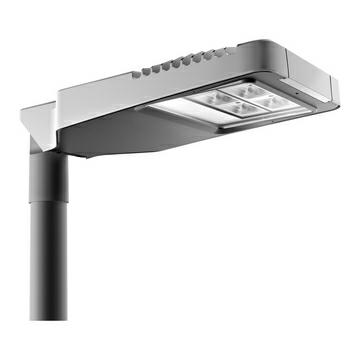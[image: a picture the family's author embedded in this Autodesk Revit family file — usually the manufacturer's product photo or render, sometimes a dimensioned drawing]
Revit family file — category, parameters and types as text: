
# Revit family: Lighting-StreetLighting-GEWISS-ROAD[5]MEDIUM-LED_OPTIC_WIDE-W_NEMA-ZAGA
name_source: partatom
category: Apparecchi per illuminazione
units: mm (PartAtom-declared; Revit-internal decimal feet)

## family parameters
Basato su piano di lavoro = No
Condiviso = No
Punto di calcolo locali = No
Quota connettore circolare = Usa diametro
Sempre verticale = Sì
Sorgente d'illuminazione = No
Taglio con vuoti quando caricato = No
Tipo di parte = Normale

## types (4) — shared parameters
Applicazione = External
Body = Die-cast aluminium -
Catalogue = LIGHTING
Catalogue Range = ROAD [5]
Classification: = -
Color Rendering Index = CRI-70
Colore = Graphite grey
Colour : = Powder coating
Colour temperature = 4000K
Colour temperature: = 4000 K (CRI>70)
Context = Street and parking lighting
DIN 18032-3 certification = -
Device with reduced surface temperature = -
Driver = Included
Driver Box = Built-in
Electrocod = 244C
Eletrical and lighting features = -
External screw = Stainless steel
Fixing = Pole Head - Outreach
Gasket = Anti-aging silicone
General information = -
Glow Wire Test : = -
IDF = ebad91c9-d513-4bb5-a7ee-f89ce0000d46
IDT = d586ed85c3ba44b3a220029348af3ca9
IP degree = IP66
Immagine tipo = GWR5276M.jpg
Installationa and maintenance = -
Insulation class = II
LED Life time (L80B10) = 100000H
LED Maintenance = Not available
LED current. = 0,5A
Lamp- = LED
Lampada = LED
Lifetime = L90B10 (Tq+25°C) = 100.000 h
Locking Hook = Integrated front handle
Luminaire = LED Road Equipment
Materials = -
Maximum surface exposed to the wind = 0,19M2
Maximum surface exposed to the wind : = 0.19 m2
Minimum distance from the illuminated object = 1M
Mouting and installation = Pole Head - Outreach
Operating temperature : = -25 +30 °C
Operating temperature: = -25 +30 °C
Optic = WIDE
Optic : = Metallized polycarbonate reflector
Optic Maintenance = Not available
Optic and illuminating features = -
Overvoltage protection = DM 10KV / CM 10KV
Overvoltage resistance = 10 KV (Common mode)
Photobiological Risk Class = RG0
Produttore = GEWISS S.p.A.
Rated frequency (Hz) = 50 / 60
SEO = Street lighting
Shield type = 4mm thick flat tempered glass
Shock resistance = IK08
Standard Deviation Colour Matching = SDCM = 5
Standard- = EN 60598-2-3, EN 60598-1 IEC/TR 62778
Standards and approvals = -
Stocking temperature = -
Supply voltage = 220 - 240 V
Technical sheet = https://www.gewiss.com
Tilt adjustable = -20° ÷ +10° side bracket - -10° ÷ +20° pole head
Tilt- = -20° ÷ +10° side bracket - -10° ÷ +20° pole head
Tipo alimentatore = Constant Current Driver Led
Tipologia = Bi power
Type of light source = LED - Not replaceable
URL = https://www.gewiss.com
Unified Glare Rating = G*4 - ULOR = 0
Unique digital code (Datamatrix) = Currently not present
Version file RFA = 20.11
Voltage- = 220 / 240 V - 50 / 60 Hz
Warranty = 5 years
Wiring = Isolating switch

## per-type parameters (varying)
| type | Control System | Efficiency (lm/W) | IPEA | Lumen output (lm) | Modello | Number of modules | System power | System power : | Weight (kg): |
| GWR5254ZW - ROAD5 MEDI WIDE 4M 4000K 0,50A CL2 W ZHA | Remote management with Zhaga module | 110 | ROAD = A + // LARGE AREAS = A4 + // CYCLOPEDONALS = A + // GREEN AREAS = A + // HISTORICAL CENTER = A5 + | 16100 | GWR5254ZW | 4 (4x3 LED) | 146W | 146 W @ 0.5A | 8,4 |
| GWR5254NW - ROAD5 MEDI WIDE 4M 4000K 0,50A CL2 W NEM | Remote management with Nema module | 110 | ROAD = A + // LARGE AREAS = A4 + // CYCLOPEDONALS = A + // GREEN AREAS = A + // HISTORICAL CENTER = A5 + | 16100 | GWR5254NW | 4 (4x3 LED) | 146W | 146 W @ 0.5A | 8,4 |
| GWR5253ZW - ROAD5 MEDI WIDE 3M 4000K 0,50A CL2 W ZHA | Remote management with Zhaga module | 112 | ROAD = A ++ // LARGE AREAS = A4 + // CYCLOPEDONALS = A ++ // GREEN AREAS = A ++ // HISTORICAL CENTER = A6 + | 12200 | GWR5253ZW | 3 (3x3 LED) | 109W | 109 W @ 0.5A | 8 |
| GWR5253NW - ROAD5 MEDI WIDE 3M 4000K 0,50A CL2 W NEM | Remote management with Nema module | 112 | ROAD = A ++ // LARGE AREAS = A4 + // CYCLOPEDONALS = A ++ // GREEN AREAS = A ++ // HISTORICAL CENTER = A6 + | 12200 | GWR5253NW | 3 (3x3 LED) | 109W | 109 W @ 0.5A | 8 |

note: column(s) folded — value = type name in every type: Descrizione

## geometry (parser evidence)
native form markers: Blend x2
no freeform markers — native parametric forms only
